# Revit family: SFRI
name_source: partatom
category: Air Terminals
revit_build: Autodesk Revit MEP 2012 (Build: 20110309_2315(x64)
units: mm (PartAtom-declared; Revit-internal decimal feet)

## types (7) — shared parameters
Central = 3"
Manufacturer = INNES
Máxima presión estática = 0.00 in-wg
Máxima velocidad de cuello = 0 FPM
Mínima presión estática = 0.00 in-wg
Mínima velocidad de cuello = 0 FPM
URL = http://www.innes.com.mx

## per-type parameters (varying)
| type | A cuello | B plato | Cuello1 | Perfil 1 | Perfil 2 | Plato |
| SFRI-C-24-30 | 23 15/16" | 29 3/4" | 24" | Yes | Yes | 30" |
| SFRI-C-21-27 | 20 15/16" | 26 3/4" | 21" | Yes | Yes | 27" |
| SFRI-C-18-24 | 17 15/16" | 23 3/4" | 18" | Yes | Yes | 24" |
| SFRI-C-15-21 | 14 15/16" | 20 3/4" | 15" | Yes | Yes | 21" |
| SFRI-C-12-18 | 11 15/16" | 17 3/4" | 12" | Yes | Yes | 18" |
| SFRI-C-09-15 | 8 15/16" | 14 3/4" | 9" | Yes | Yes | 15" |
| SFRI-C-06-12 | 5 15/16" | 11 3/4" | 6" | No | No | 12" |

## geometry (parser evidence)
native form markers: Sweep x1
no freeform markers — native parametric forms only
